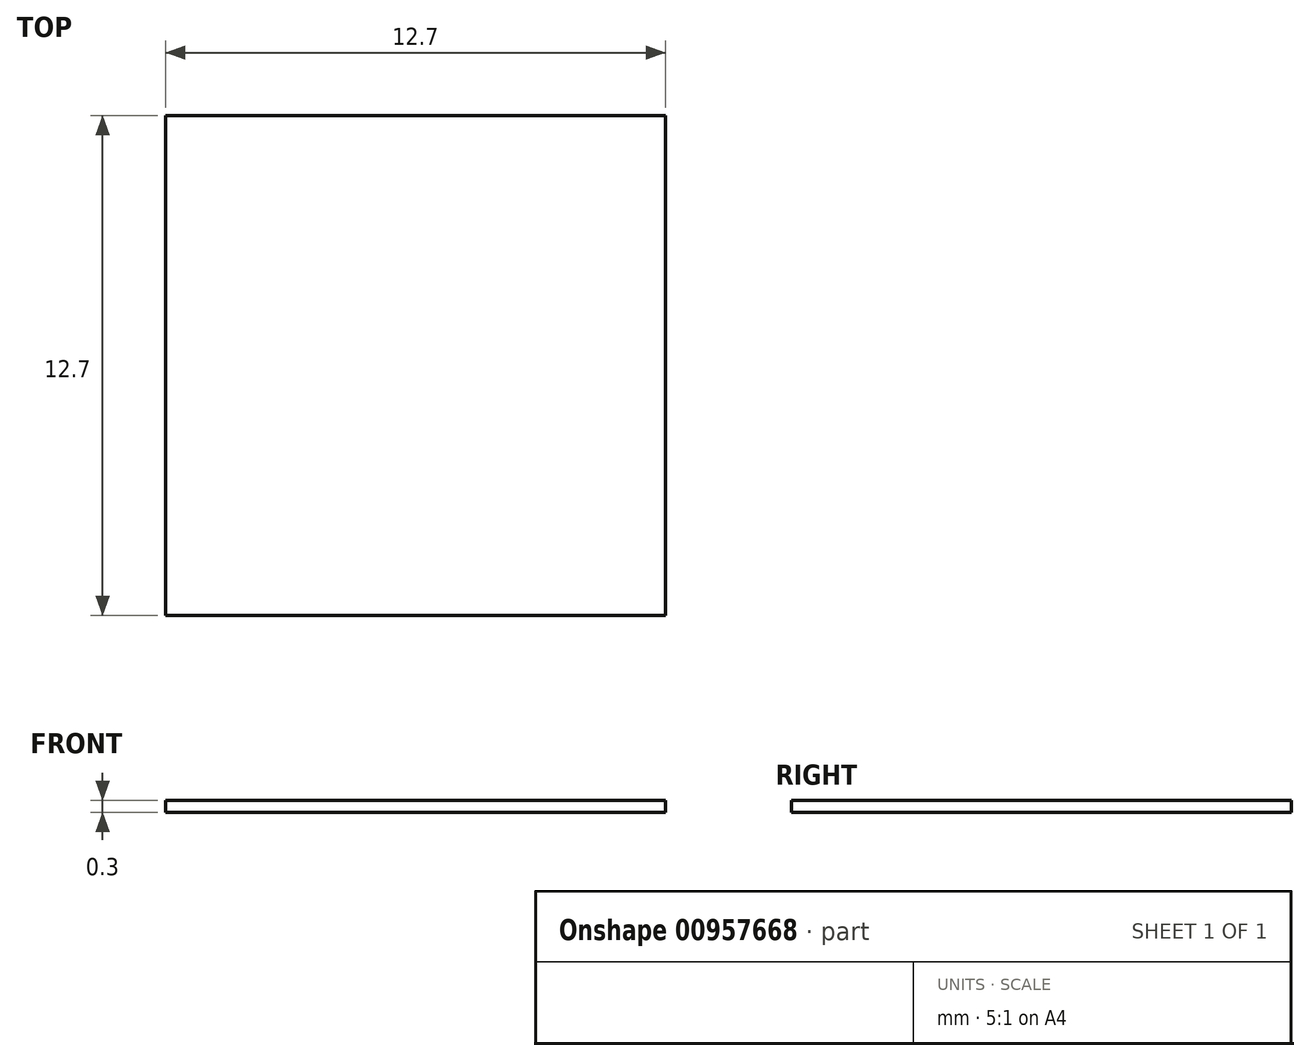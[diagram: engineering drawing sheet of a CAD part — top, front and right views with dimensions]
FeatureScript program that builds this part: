
annotation { "Feature Type Name" : "Feature", "Feature Type Description" : "" }
export const myFeature = defineFeature(function(context is Context, id is Id, definition is map)
    precondition{}
    {
        {
            var Q0;
            Q0=qCreatedBy(makeId("Top.planeOp"),FACE);
            var sketch = newSketch(context, id + "F0", { "sketchPlane" : qUnion([Q0])});
            skLineSegment(sketch, "E0.bottom", {"start": v(6.35, 6.35) * mm, "end": v(-6.35, 6.35) * mm});
            skLineSegment(sketch, "E0.top", {"start": v(6.35, -6.35) * mm, "end": v(-6.35, -6.35) * mm});
            skLineSegment(sketch, "E0.left", {"start": v(6.35, 6.35) * mm, "end": v(6.35, -6.35) * mm});
            skLineSegment(sketch, "E0.right", {"start": v(-6.35, 6.35) * mm, "end": v(-6.35, -6.35) * mm});
            skPoint(sketch, "E0.middle", {"position": v(0, 0) * mm});
            skSolve(sketch);
        }
        {
            var Q0;
            Q0 = qSketchRegion(id + "F0", true);
            extrude(context, id + "F1", {"entities" : qUnion([Q0]), "depth" : .3 * mm, "offsetDistance" : 25.4 * mm});
        }
        {
            var Q0;
            Q0=makeQuery(id+"F1.opExtrude","CAP_EDGE",EDGE,{"disambiguationData":[OSD([sQuery(id+"F0.wireOp",EDGE,"E0.right")])],"isStart":false});
            cPoint(context, id + "F2", {"entities" : qUnion([Q0]), "parameter" : 0.5});
        }
        {
            var Q0;
            Q0 = qCreatedBy(id + "F2" ,VERTEX);
            var Q1;
            Q1=makeQuery(id+"F1.opExtrude","CAP_VERTEX",VERTEX,{"disambiguationData":[OSD([sQuery(id+"F0.wireOp",EDGE,"E0.top"),sQuery(id+"F0.wireOp",EDGE,"E0.left")])],"isStart":false});
            var Q2;
            Q2=makeQuery(id+"F1.opExtrude","CAP_VERTEX",VERTEX,{"disambiguationData":[OSD([sQuery(id+"F0.wireOp",EDGE,"E0.bottom"),sQuery(id+"F0.wireOp",EDGE,"E0.left")])],"isStart":false});
            cPlane(context, id + "F3", {"entities" : qUnion([Q0, Q1, Q2]), "cplaneType" : CPlaneType.THREE_POINT, "offset" : 25.4 * mm, "width" : 152.4 * mm, "height" : 152.4 * mm});
        }
    });
